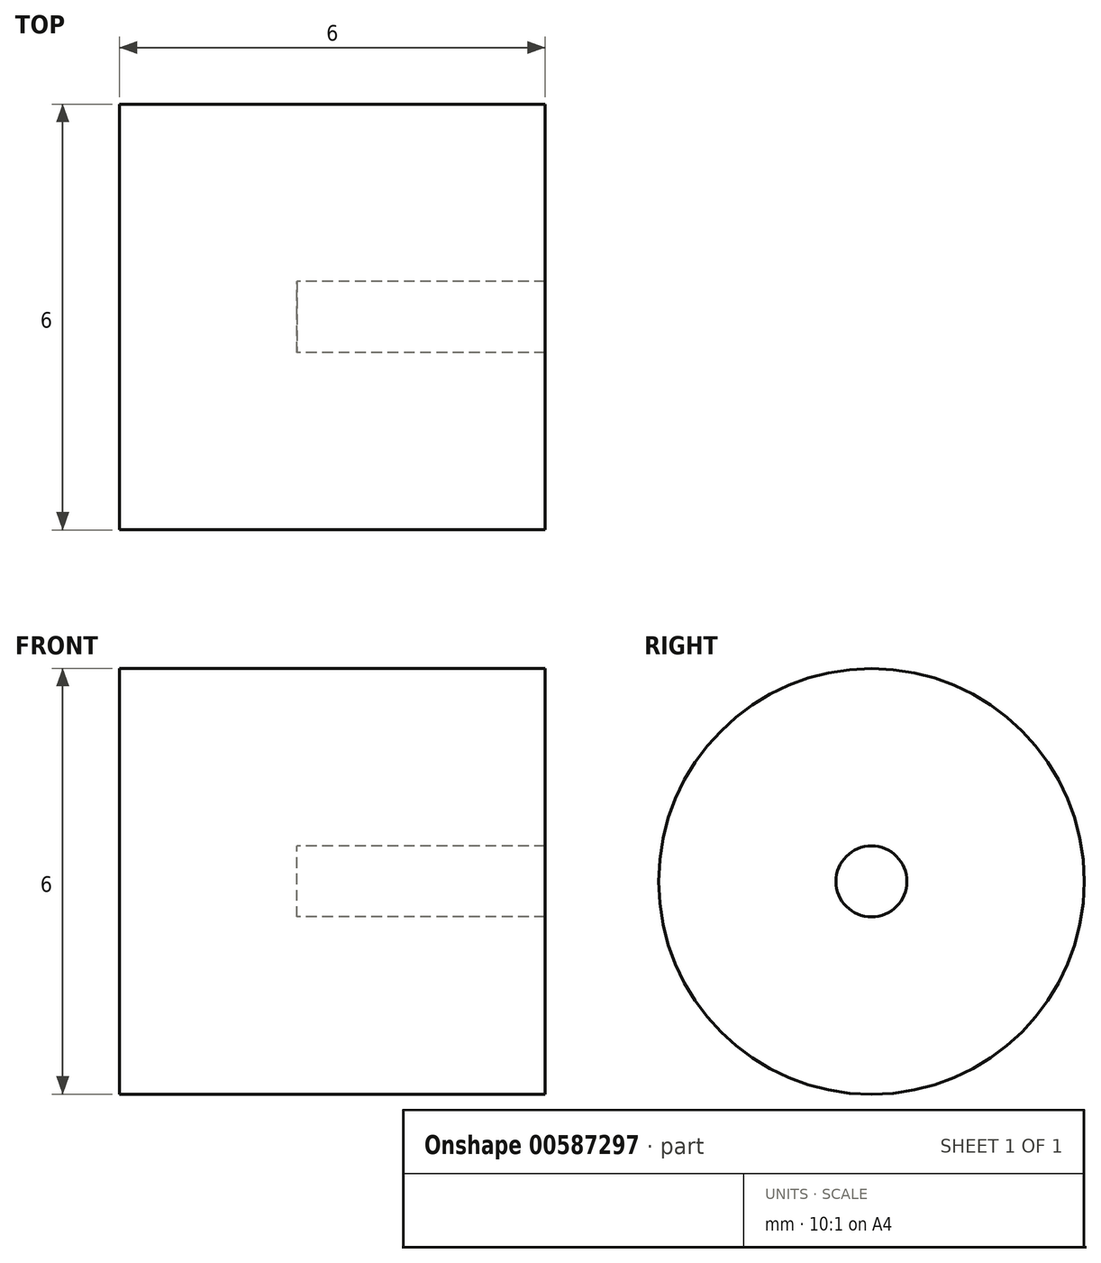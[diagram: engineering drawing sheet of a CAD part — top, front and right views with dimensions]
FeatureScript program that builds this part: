
annotation { "Feature Type Name" : "Feature", "Feature Type Description" : "" }
export const myFeature = defineFeature(function(context is Context, id is Id, definition is map)
    precondition{}
    {
        {
            var Q0;
            Q0=qCreatedBy(makeId("Right.planeOp"),FACE);
            var sketch = newSketch(context, id + "F0", { "sketchPlane" : qUnion([Q0])});
            skCircle(sketch, "E0", {"center": v(-6.66, 10.7) * mm, "radius": 3 * mm});
            skSolve(sketch);
        }
        {
            var Q0;
            Q0=makeQuery(id+"F0.imprint","IMPRINT",FACE,{"disambiguationData":[TD([[makeQuery(id+"F0.imprint","IMPRINT",EDGE,{"derivedFrom":sQuery(id+"F0.wireOp",EDGE,"E0")}),1.0]])]});
            extrude(context, id + "F1", {"entities" : qUnion([Q0]), "depth" : 6 * mm, "offsetDistance" : 25 * mm});
        }
        {
            var Q0;
            Q0=makeQuery(id+"F1.opExtrude","CAP_FACE",FACE,{"disambiguationData":[OSD([sQuery(id+"F0.wireOp",EDGE,"E0")])],"isStart":false});
            shell(context, id + "F2", {"entities" : qUnion([Q0]), "thickness" : 2.5 * mm});
        }
    });
